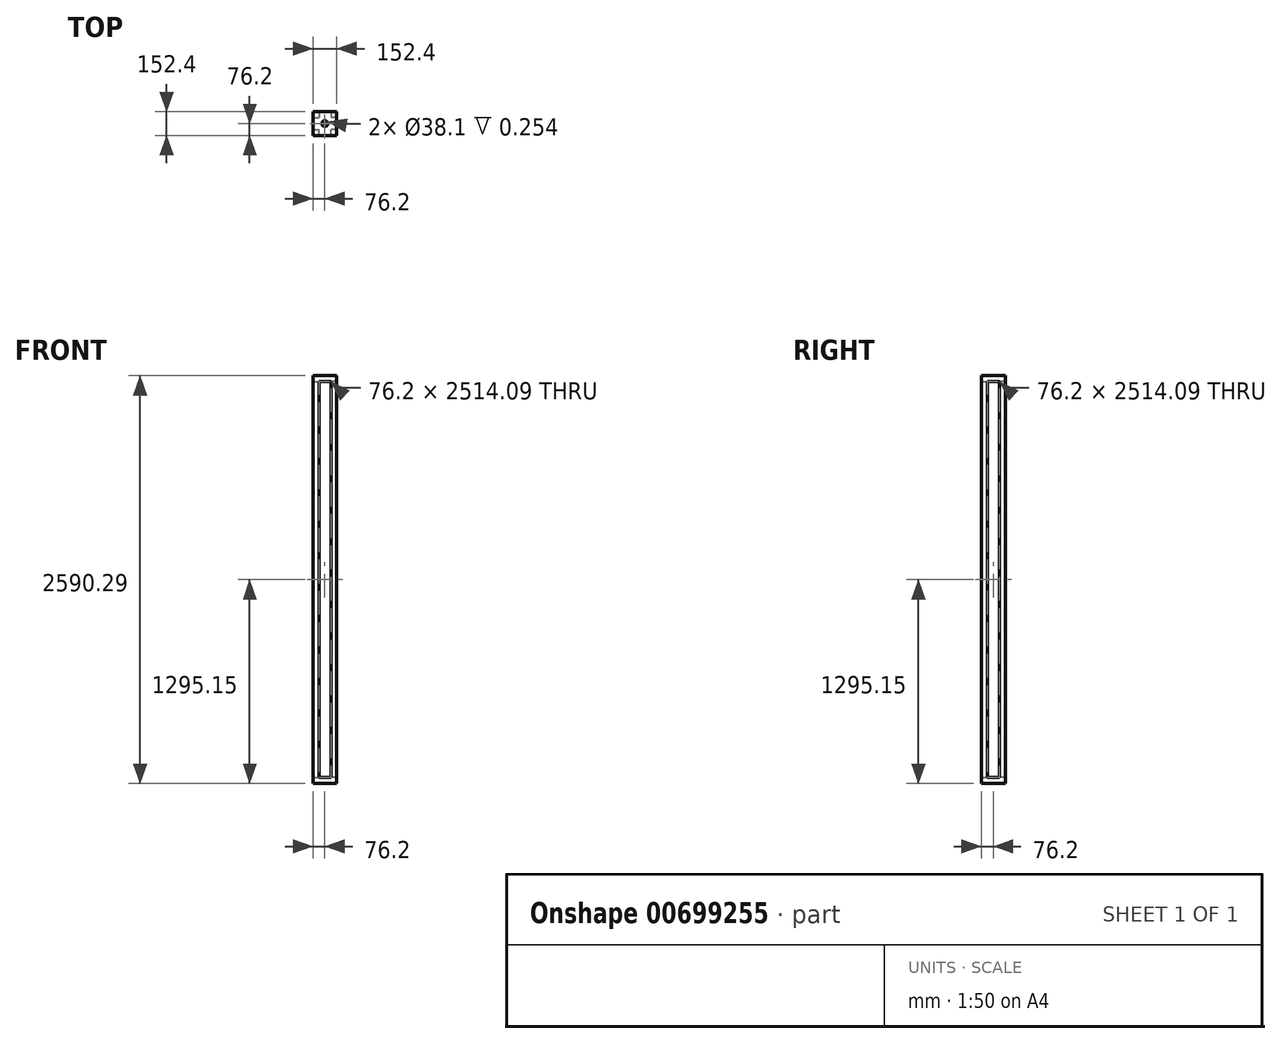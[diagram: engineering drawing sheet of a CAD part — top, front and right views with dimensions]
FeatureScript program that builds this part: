
annotation { "Feature Type Name" : "Feature", "Feature Type Description" : "" }
export const myFeature = defineFeature(function(context is Context, id is Id, definition is map)
    precondition{}
    {
        {
            var Q0;
            Q0=qCreatedBy(makeId("Top.planeOp"),FACE);
            var sketch = newSketch(context, id + "F0", { "sketchPlane" : qUnion([Q0])});
            skLineSegment(sketch, "E0.bottom", {"start": v(76.2, -76.2) * mm, "end": v(-76.2, -76.2) * mm});
            skLineSegment(sketch, "E0.top", {"start": v(76.2, 76.2) * mm, "end": v(-76.2, 76.2) * mm});
            skLineSegment(sketch, "E0.left", {"start": v(76.2, -76.2) * mm, "end": v(76.2, 76.2) * mm});
            skLineSegment(sketch, "E0.right", {"start": v(-76.2, -76.2) * mm, "end": v(-76.2, 76.2) * mm});
            skPoint(sketch, "E0.middle", {"position": v(0, 0) * mm});
            skSolve(sketch);
        }
        {
            var Q0;
            Q0 = qSketchRegion(id + "F0", true);
            extrude(context, id + "F1", {"entities" : qUnion([Q0]), "oppositeDirection" : true, "depth" : 38.1 * mm, "offsetDistance" : 25.4 * mm});
        }
        {
            var Q0;
            Q0=makeQuery(id+"F1.opExtrude","CAP_FACE",FACE,{"disambiguationData":[OSD([sQuery(id+"F0.wireOp",EDGE,"E0.bottom"),sQuery(id+"F0.wireOp",EDGE,"E0.top"),sQuery(id+"F0.wireOp",EDGE,"E0.left"),sQuery(id+"F0.wireOp",EDGE,"E0.right")])],"isStart":true});
            var sketch = newSketch(context, id + "F2", { "sketchPlane" : qUnion([Q0])});
            skLineSegment(sketch, "E1.bottom", {"start": v(76.2, -76.2) * mm, "end": v(38.1, -76.2) * mm});
            skLineSegment(sketch, "E1.top", {"start": v(76.2, -38.1) * mm, "end": v(38.1, -38.1) * mm});
            skLineSegment(sketch, "E1.left", {"start": v(76.2, -76.2) * mm, "end": v(76.2, -38.1) * mm});
            skLineSegment(sketch, "E1.right", {"start": v(38.1, -76.2) * mm, "end": v(38.1, -38.1) * mm});
            skLineSegment(sketch, "E2.bottom", {"start": v(76.2, 76.2) * mm, "end": v(38.1, 76.2) * mm});
            skLineSegment(sketch, "E2.top", {"start": v(76.2, 38.1) * mm, "end": v(38.1, 38.1) * mm});
            skLineSegment(sketch, "E2.left", {"start": v(76.2, 76.2) * mm, "end": v(76.2, 38.1) * mm});
            skLineSegment(sketch, "E2.right", {"start": v(38.1, 76.2) * mm, "end": v(38.1, 38.1) * mm});
            skLineSegment(sketch, "E3.bottom", {"start": v(-76.2, -76.2) * mm, "end": v(-38.1, -76.2) * mm});
            skLineSegment(sketch, "E3.top", {"start": v(-76.2, -38.1) * mm, "end": v(-38.1, -38.1) * mm});
            skLineSegment(sketch, "E3.left", {"start": v(-76.2, -76.2) * mm, "end": v(-76.2, -38.1) * mm});
            skLineSegment(sketch, "E3.right", {"start": v(-38.1, -76.2) * mm, "end": v(-38.1, -38.1) * mm});
            skLineSegment(sketch, "E4.bottom", {"start": v(-76.2, 76.2) * mm, "end": v(-38.1, 76.2) * mm});
            skLineSegment(sketch, "E4.top", {"start": v(-76.2, 38.1) * mm, "end": v(-38.1, 38.1) * mm});
            skLineSegment(sketch, "E4.left", {"start": v(-76.2, 76.2) * mm, "end": v(-76.2, 38.1) * mm});
            skLineSegment(sketch, "E4.right", {"start": v(-38.1, 76.2) * mm, "end": v(-38.1, 38.1) * mm});
            skSolve(sketch);
        }
        {
            var Q0;
            Q0 = qSketchRegion(id + "F2", true);
            extrude(context, id + "F3", {"entities" : qUnion([Q0]), "operationType" : NewBodyOperationType.ADD, "depth" : 2514.1 * mm, "offsetDistance" : 25.4 * mm});
        }
        {
            var Q0;
            Q0=makeQuery(id+"F3.opExtrude","CAP_FACE",FACE,{"disambiguationData":[OSD([sQuery(id+"F2.wireOp",EDGE,"E4.bottom"),sQuery(id+"F2.wireOp",EDGE,"E4.top"),sQuery(id+"F2.wireOp",EDGE,"E4.left"),sQuery(id+"F2.wireOp",EDGE,"E4.right")])],"isStart":false});
            var sketch = newSketch(context, id + "F4", { "sketchPlane" : qUnion([Q0])});
            skLineSegment(sketch, "E5.bottom", {"start": v(-76.2, 76.2) * mm, "end": v(76.2, 76.2) * mm});
            skLineSegment(sketch, "E5.top", {"start": v(-76.2, -76.2) * mm, "end": v(76.2, -76.2) * mm});
            skLineSegment(sketch, "E5.left", {"start": v(-76.2, 76.2) * mm, "end": v(-76.2, -76.2) * mm});
            skLineSegment(sketch, "E5.right", {"start": v(76.2, 76.2) * mm, "end": v(76.2, -76.2) * mm});
            skSolve(sketch);
        }
        {
            var Q0;
            Q0 = qSketchRegion(id + "F4", true);
            extrude(context, id + "F5", {"entities" : qUnion([Q0]), "operationType" : NewBodyOperationType.ADD, "depth" : 38.1 * mm, "offsetDistance" : 25.4 * mm});
        }
        {
            var Q0;
            Q0=makeQuery(id+"F5.opExtrude","CAP_FACE",FACE,{"disambiguationData":[OSD([sQuery(id+"F4.wireOp",EDGE,"E5.bottom"),sQuery(id+"F4.wireOp",EDGE,"E5.top"),sQuery(id+"F4.wireOp",EDGE,"E5.left"),sQuery(id+"F4.wireOp",EDGE,"E5.right")])],"isStart":false});
            var sketch = newSketch(context, id + "F6", { "sketchPlane" : qUnion([Q0])});
            skCircle(sketch, "E6", {"center": v(0, 0) * mm, "radius": 19.05 * mm});
            skSolve(sketch);
        }
        {
            var Q0;
            Q0=makeQuery(id+"F6.imprint","IMPRINT",FACE,{"disambiguationData":[TD([[makeQuery(id+"F6.imprint","IMPRINT",EDGE,{"derivedFrom":sQuery(id+"F6.wireOp",EDGE,"E6")}),1.0]])]});
            extrude(context, id + "F7", {"entities" : qUnion([Q0]), "operationType" : NewBodyOperationType.REMOVE, "oppositeDirection" : true, "depth" : 0.25 * mm, "offsetDistance" : 25.4 * mm});
        }
        {
            var Q0;
            Q0=makeQuery(id+"F1.opExtrude","CAP_FACE",FACE,{"disambiguationData":[OSD([sQuery(id+"F0.wireOp",EDGE,"E0.bottom"),sQuery(id+"F0.wireOp",EDGE,"E0.top"),sQuery(id+"F0.wireOp",EDGE,"E0.left"),sQuery(id+"F0.wireOp",EDGE,"E0.right")])],"isStart":false});
            var sketch = newSketch(context, id + "F8", { "sketchPlane" : qUnion([Q0])});
            skCircle(sketch, "E7", {"center": v(0, 0) * mm, "radius": 19.05 * mm});
            skSolve(sketch);
        }
        {
            var Q0;
            Q0=makeQuery(id+"F8.imprint","IMPRINT",FACE,{"disambiguationData":[TD([[makeQuery(id+"F8.imprint","IMPRINT",EDGE,{"derivedFrom":sQuery(id+"F8.wireOp",EDGE,"E7")}),1.0]])]});
            extrude(context, id + "F9", {"entities" : qUnion([Q0]), "operationType" : NewBodyOperationType.REMOVE, "oppositeDirection" : true, "depth" : 0.25 * mm, "offsetDistance" : 25.4 * mm});
        }
    });
